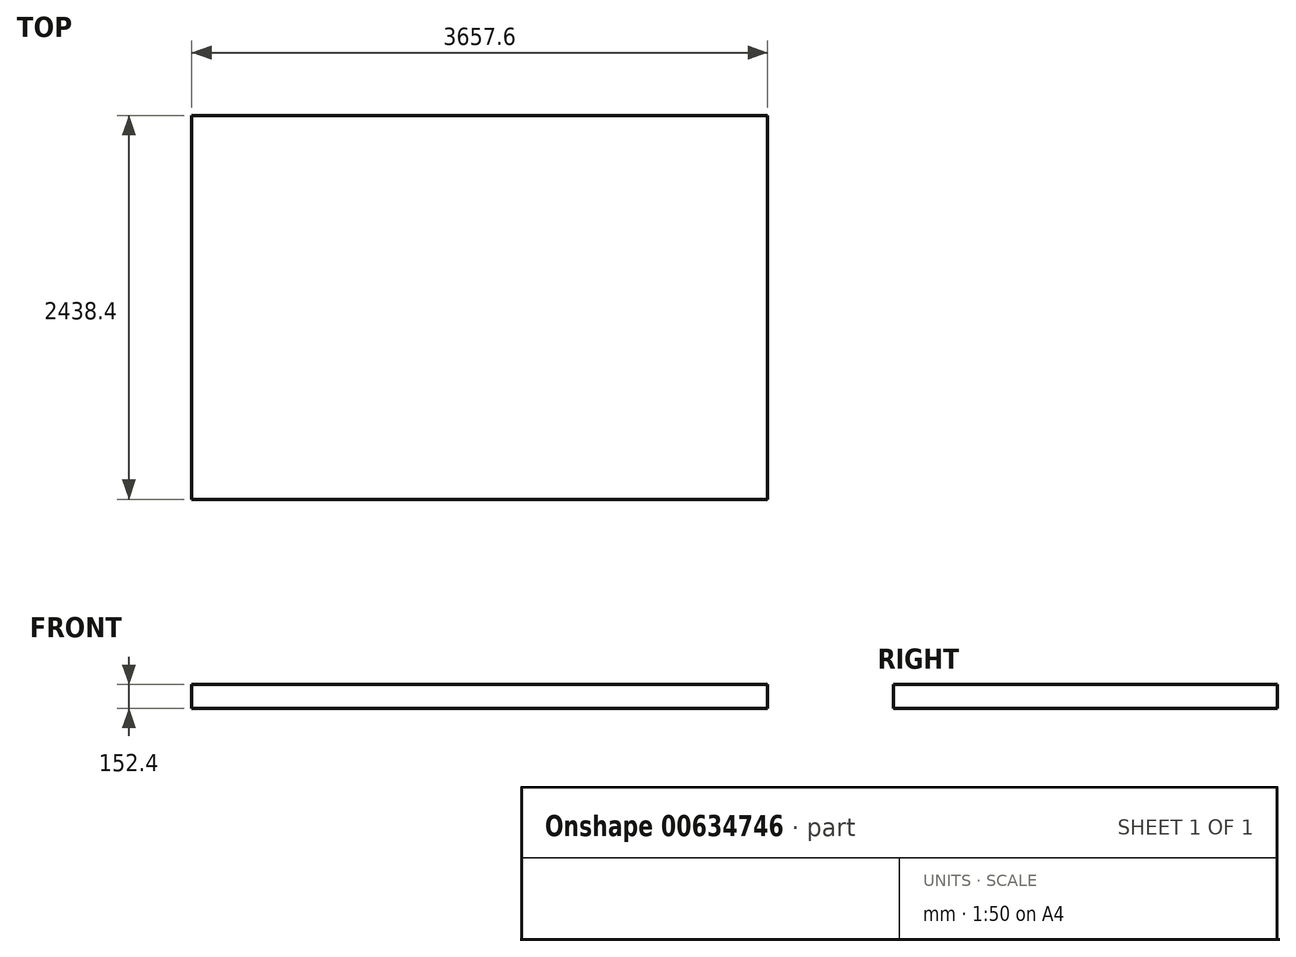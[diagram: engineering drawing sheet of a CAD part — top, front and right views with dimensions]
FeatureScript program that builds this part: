
annotation { "Feature Type Name" : "Feature", "Feature Type Description" : "" }
export const myFeature = defineFeature(function(context is Context, id is Id, definition is map)
    precondition{}
    {
        {
            var Q0;
            Q0=qCreatedBy(makeId("Top.planeOp"),FACE);
            var sketch = newSketch(context, id + "F0", { "sketchPlane" : qUnion([Q0])});
            skLineSegment(sketch, "E0.bottom", {"start": v(-2349.25, 754.97) * mm, "end": v(1308.35, 754.97) * mm});
            skLineSegment(sketch, "E0.top", {"start": v(-2349.25, -1683.43) * mm, "end": v(1308.35, -1683.43) * mm});
            skLineSegment(sketch, "E0.left", {"start": v(-2349.25, 754.97) * mm, "end": v(-2349.25, -1683.43) * mm});
            skLineSegment(sketch, "E0.right", {"start": v(1308.35, 754.97) * mm, "end": v(1308.35, -1683.43) * mm});
            skLineSegment(sketch, "E1.bottom", {"start": v(-2349.25, 754.97) * mm, "end": v(-2247.65, 754.97) * mm, "construction": true});
            skLineSegment(sketch, "E1.top", {"start": v(-2349.25, 653.37) * mm, "end": v(-2247.65, 653.37) * mm, "construction": true});
            skLineSegment(sketch, "E1.left", {"start": v(-2349.25, 754.97) * mm, "end": v(-2349.25, 653.37) * mm, "construction": true});
            skLineSegment(sketch, "E1.right", {"start": v(-2247.65, 754.97) * mm, "end": v(-2247.65, 653.37) * mm, "construction": true});
            skLineSegment(sketch, "E2.bottom", {"start": v(-2349.25, -1683.43) * mm, "end": v(-2247.65, -1683.43) * mm, "construction": true});
            skLineSegment(sketch, "E2.top", {"start": v(-2349.25, -1581.83) * mm, "end": v(-2247.65, -1581.83) * mm, "construction": true});
            skLineSegment(sketch, "E2.left", {"start": v(-2349.25, -1683.43) * mm, "end": v(-2349.25, -1581.83) * mm, "construction": true});
            skLineSegment(sketch, "E2.right", {"start": v(-2247.65, -1683.43) * mm, "end": v(-2247.65, -1581.83) * mm, "construction": true});
            skLineSegment(sketch, "E3.bottom", {"start": v(1308.35, -1683.43) * mm, "end": v(1206.75, -1683.43) * mm, "construction": true});
            skLineSegment(sketch, "E3.top", {"start": v(1308.35, -1581.83) * mm, "end": v(1206.75, -1581.83) * mm, "construction": true});
            skLineSegment(sketch, "E3.left", {"start": v(1308.35, -1683.43) * mm, "end": v(1308.35, -1581.83) * mm, "construction": true});
            skLineSegment(sketch, "E3.right", {"start": v(1206.75, -1683.43) * mm, "end": v(1206.75, -1581.83) * mm, "construction": true});
            skLineSegment(sketch, "E4.bottom", {"start": v(1308.35, 754.97) * mm, "end": v(1206.75, 754.97) * mm, "construction": true});
            skLineSegment(sketch, "E4.top", {"start": v(1308.35, 653.37) * mm, "end": v(1206.75, 653.37) * mm, "construction": true});
            skLineSegment(sketch, "E4.left", {"start": v(1308.35, 754.97) * mm, "end": v(1308.35, 653.37) * mm, "construction": true});
            skLineSegment(sketch, "E4.right", {"start": v(1206.75, 754.97) * mm, "end": v(1206.75, 653.37) * mm, "construction": true});
            skSolve(sketch);
        }
        {
            var Q0;
            Q0 = qSketchRegion(id + "F0", true);
            extrude(context, id + "F1", {"entities" : qUnion([Q0]), "depth" : 152.4 * mm, "offsetDistance" : 30.48 * mm});
        }
    });
